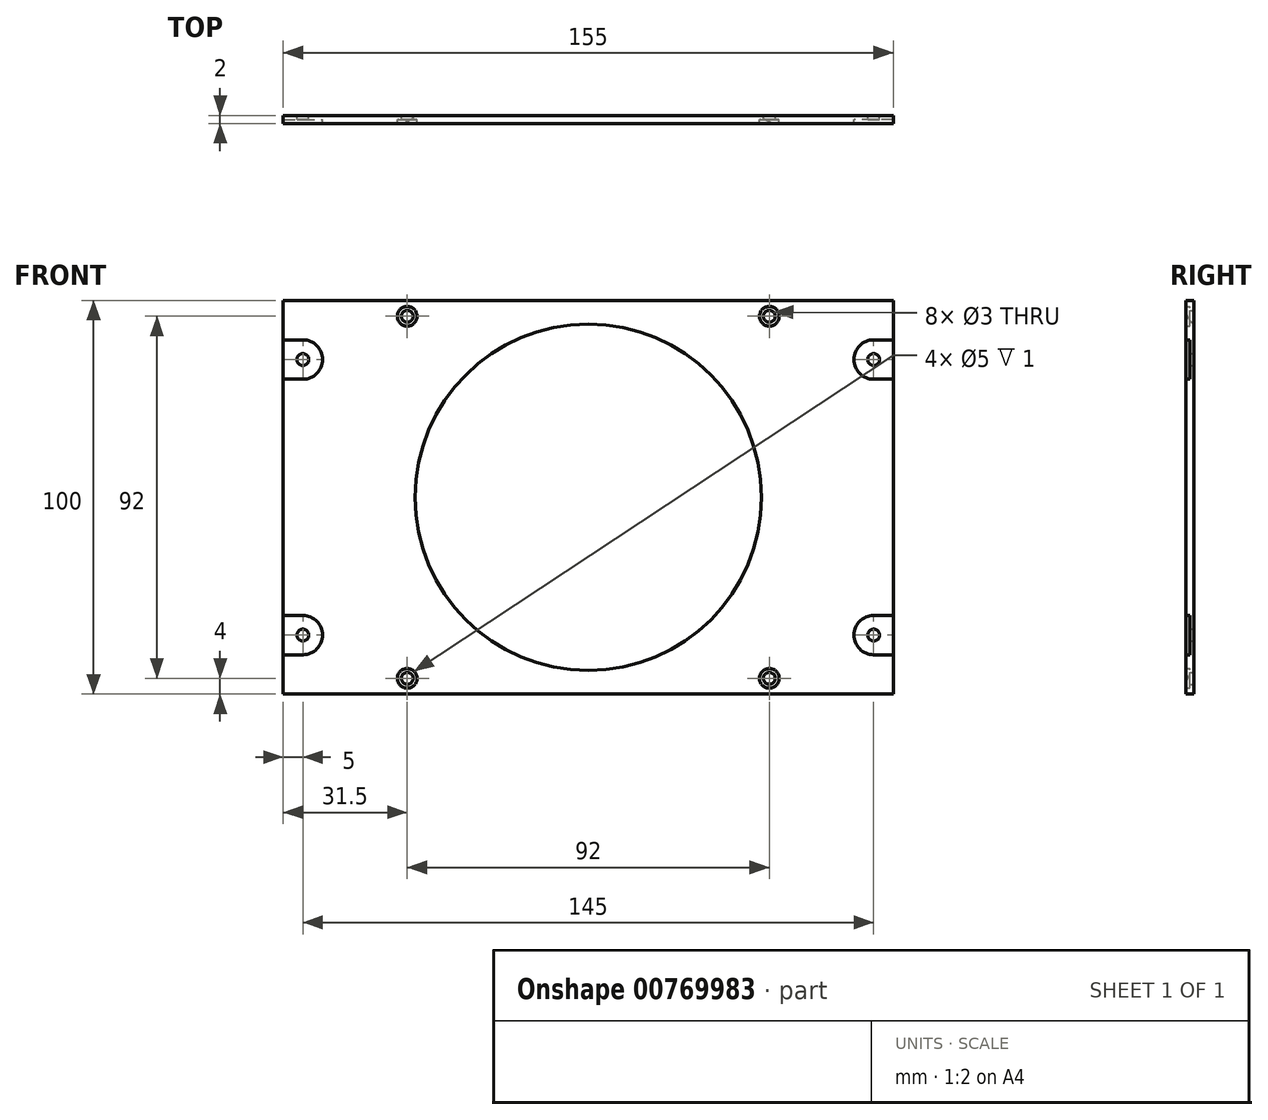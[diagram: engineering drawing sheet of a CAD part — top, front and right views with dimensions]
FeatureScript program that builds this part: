
annotation { "Feature Type Name" : "Feature", "Feature Type Description" : "" }
export const myFeature = defineFeature(function(context is Context, id is Id, definition is map)
    precondition{}
    {
        {
            var Q0;
            Q0=qCreatedBy(makeId("Front.planeOp"),FACE);
            var sketch = newSketch(context, id + "F0", { "sketchPlane" : qUnion([Q0])});
            skLineSegment(sketch, "E0.bottom", {"start": v(77.5, -50) * mm, "end": v(-77.5, -50) * mm});
            skLineSegment(sketch, "E0.top", {"start": v(77.5, 50) * mm, "end": v(-77.5, 50) * mm});
            skLineSegment(sketch, "E0.left", {"start": v(77.5, -50) * mm, "end": v(77.5, 50) * mm});
            skLineSegment(sketch, "E0.right", {"start": v(-77.5, -50) * mm, "end": v(-77.5, 50) * mm});
            skPoint(sketch, "E0.middle", {"position": v(0, 0) * mm});
            skCircle(sketch, "E1", {"center": v(0, 0) * mm, "radius": 44 * mm});
            skLineSegment(sketch, "E2.bottom", {"start": v(46, -46) * mm, "end": v(-46, -46) * mm});
            skLineSegment(sketch, "E2.top", {"start": v(46, 46) * mm, "end": v(-46, 46) * mm});
            skLineSegment(sketch, "E2.left", {"start": v(46, -46) * mm, "end": v(46, 46) * mm});
            skLineSegment(sketch, "E2.right", {"start": v(-46, -46) * mm, "end": v(-46, 46) * mm});
            skCircle(sketch, "E3", {"center": v(-46, 46) * mm, "radius": 1.5 * mm});
            skCircle(sketch, "E4", {"center": v(46, 46) * mm, "radius": 1.5 * mm});
            skCircle(sketch, "E5", {"center": v(46, -46) * mm, "radius": 1.5 * mm});
            skCircle(sketch, "E6", {"center": v(-46, -46) * mm, "radius": 1.5 * mm});
            skLineSegment(sketch, "E7.bottom", {"start": v(-77.5, 40) * mm, "end": v(-72.5, 40) * mm});
            skLineSegment(sketch, "E7.top", {"start": v(-77.5, 30) * mm, "end": v(-72.5, 30) * mm});
            skLineSegment(sketch, "E7.left", {"start": v(-77.5, 40) * mm, "end": v(-77.5, 30) * mm});
            skArc(sketch, "E8", {"start": v(-72.5, 40) * mm, "mid": v(-67.5, 35) * mm, "end": v(-72.5, 30) * mm});
            skLineSegment(sketch, "E9.MirrorCS", {"start": v(-77.5, -30) * mm, "end": v(-72.5, -30) * mm});
            skLineSegment(sketch, "E10.MirrorCS", {"start": v(-77.5, -40) * mm, "end": v(-72.5, -40) * mm});
            skArc(sketch, "E11.MirrorCS", {"start": v(-72.5, -40) * mm, "mid": v(-67.5, -35) * mm, "end": v(-72.5, -30) * mm});
            skLineSegment(sketch, "E12.MirrorCS", {"start": v(77.5, 40) * mm, "end": v(72.5, 40) * mm});
            skArc(sketch, "E13.MirrorCS", {"start": v(72.5, 40) * mm, "mid": v(67.5, 35) * mm, "end": v(72.5, 30) * mm});
            skLineSegment(sketch, "E14.MirrorCS", {"start": v(77.5, 30) * mm, "end": v(72.5, 30) * mm});
            skLineSegment(sketch, "E15.MirrorCS", {"start": v(77.5, -30) * mm, "end": v(72.5, -30) * mm});
            skLineSegment(sketch, "E16.MirrorCS", {"start": v(77.5, -40) * mm, "end": v(72.5, -40) * mm});
            skArc(sketch, "E17.MirrorCS", {"start": v(72.5, -40) * mm, "mid": v(67.5, -35) * mm, "end": v(72.5, -30) * mm});
            skCircle(sketch, "E18", {"center": v(-72.5, 35) * mm, "radius": 1.5 * mm});
            skCircle(sketch, "E19.MirrorC", {"center": v(-72.5, -35) * mm, "radius": 1.5 * mm});
            skCircle(sketch, "E20.MirrorC", {"center": v(72.5, 35) * mm, "radius": 1.5 * mm});
            skCircle(sketch, "E21.MirrorC", {"center": v(72.5, -35) * mm, "radius": 1.5 * mm});
            skCircle(sketch, "E22", {"center": v(-46, 46) * mm, "radius": 2.5 * mm});
            skCircle(sketch, "E23.MirrorC", {"center": v(-46, -46) * mm, "radius": 2.5 * mm});
            skCircle(sketch, "E24.MirrorC", {"center": v(46, -46) * mm, "radius": 2.5 * mm});
            skCircle(sketch, "E25.MirrorC", {"center": v(46, 46) * mm, "radius": 2.5 * mm});
            skSolve(sketch);
        }
        {
            var Q0;
            Q0=makeQuery(id+"F0.imprint","IMPRINT",FACE,{"disambiguationData":[TD([[makeQuery(id+"F0.imprint","IMPRINT",EDGE,{"derivedFrom":sQuery(id+"F0.wireOp",EDGE,"E0.bottom")}),-1.0]])]});
            var Q1;
            Q1=makeQuery(id+"F0.imprint","IMPRINT",FACE,{"disambiguationData":[TD([[makeQuery(id+"F0.imprint","IMPRINT",EDGE,{"derivedFrom":sQuery(id+"F0.wireOp",EDGE,"E1")}),-1.0]])]});
            extrude(context, id + "F1", {"entities" : qUnion([Q0, Q1]), "depth" : 2 * mm, "offsetDistance" : 25 * mm});
        }
        {
            var Q0;
            {var subQ0=sQuery(id+"F0.wireOp",EDGE,"E9.MirrorCS");Q0=makeQuery(id+"F0.imprint","IMPRINT",FACE,{"disambiguationData":[TD([[makeQuery(id+"F0.imprint","IMPRINT",EDGE,{"derivedFrom":subQ0}),-1.0]])]});}
            var Q1;
            Q1=makeQuery(id+"F0.imprint","IMPRINT",FACE,{"disambiguationData":[TD([[makeQuery(id+"F0.imprint","IMPRINT",EDGE,{"derivedFrom":sQuery(id+"F0.wireOp",EDGE,"E7.bottom")}),-1.0]])]});
            var Q2;
            {var subQ0=sQuery(id+"F0.wireOp",EDGE,"E12.MirrorCS");Q2=makeQuery(id+"F0.imprint","IMPRINT",FACE,{"disambiguationData":[TD([[makeQuery(id+"F0.imprint","IMPRINT",EDGE,{"derivedFrom":subQ0}),1.0]])]});}
            var Q3;
            {var subQ0=sQuery(id+"F0.wireOp",EDGE,"E15.MirrorCS");Q3=makeQuery(id+"F0.imprint","IMPRINT",FACE,{"disambiguationData":[TD([[makeQuery(id+"F0.imprint","IMPRINT",EDGE,{"derivedFrom":subQ0}),1.0]])]});}
            var Q4;
            {var subQ0=sQuery(id+"F0.wireOp",EDGE,"E22");var subQ1=sQuery(id+"F0.wireOp",EDGE,"E2.top");var subQ2=makeQuery(id+"F0.imprint","INTERSECT",VERTEX,{"derivedFrom":[subQ1,subQ0]});Q4=makeQuery(id+"F0.imprint","IMPRINT",FACE,{"disambiguationData":[TD([[makeQuery(id+"F0.imprint","IMPRINT",EDGE,{"disambiguationData":[TD([[subQ2,-1.0]])],"derivedFrom":subQ1}),-1.0]])]});}
            var Q5;
            {var subQ0=sQuery(id+"F0.wireOp",EDGE,"E22");var subQ1=sQuery(id+"F0.wireOp",EDGE,"E2.top");var subQ2=makeQuery(id+"F0.imprint","INTERSECT",VERTEX,{"derivedFrom":[subQ1,subQ0]});Q5=makeQuery(id+"F0.imprint","IMPRINT",FACE,{"disambiguationData":[TD([[makeQuery(id+"F0.imprint","IMPRINT",EDGE,{"disambiguationData":[TD([[subQ2,-1.0]])],"derivedFrom":subQ1}),1.0]])]});}
            var Q6;
            {var subQ0=sQuery(id+"F0.wireOp",EDGE,"E4");var subQ1=sQuery(id+"F0.wireOp",EDGE,"E2.top");var subQ2=makeQuery(id+"F0.imprint","INTERSECT",VERTEX,{"derivedFrom":[subQ1,subQ0]});Q6=makeQuery(id+"F0.imprint","IMPRINT",FACE,{"disambiguationData":[TD([[makeQuery(id+"F0.imprint","IMPRINT",EDGE,{"disambiguationData":[TD([[subQ2,-1.0]])],"derivedFrom":subQ1}),-1.0]])]});}
            var Q7;
            {var subQ0=sQuery(id+"F0.wireOp",EDGE,"E4");var subQ1=sQuery(id+"F0.wireOp",EDGE,"E2.top");var subQ2=makeQuery(id+"F0.imprint","INTERSECT",VERTEX,{"derivedFrom":[subQ1,subQ0]});Q7=makeQuery(id+"F0.imprint","IMPRINT",FACE,{"disambiguationData":[TD([[makeQuery(id+"F0.imprint","IMPRINT",EDGE,{"disambiguationData":[TD([[subQ2,-1.0]])],"derivedFrom":subQ1}),1.0]])]});}
            var Q8;
            {var subQ0=sQuery(id+"F0.wireOp",EDGE,"E5");var subQ1=sQuery(id+"F0.wireOp",EDGE,"E2.bottom");var subQ2=makeQuery(id+"F0.imprint","INTERSECT",VERTEX,{"derivedFrom":[subQ1,subQ0]});Q8=makeQuery(id+"F0.imprint","IMPRINT",FACE,{"disambiguationData":[TD([[makeQuery(id+"F0.imprint","IMPRINT",EDGE,{"disambiguationData":[TD([[subQ2,-1.0]])],"derivedFrom":subQ1}),1.0]])]});}
            var Q9;
            {var subQ0=sQuery(id+"F0.wireOp",EDGE,"E5");var subQ1=sQuery(id+"F0.wireOp",EDGE,"E2.bottom");var subQ2=makeQuery(id+"F0.imprint","INTERSECT",VERTEX,{"derivedFrom":[subQ1,subQ0]});Q9=makeQuery(id+"F0.imprint","IMPRINT",FACE,{"disambiguationData":[TD([[makeQuery(id+"F0.imprint","IMPRINT",EDGE,{"disambiguationData":[TD([[subQ2,-1.0]])],"derivedFrom":subQ1}),-1.0]])]});}
            var Q10;
            {var subQ0=sQuery(id+"F0.wireOp",EDGE,"E23.MirrorC");var subQ1=sQuery(id+"F0.wireOp",EDGE,"E2.bottom");var subQ2=makeQuery(id+"F0.imprint","INTERSECT",VERTEX,{"derivedFrom":[subQ1,subQ0]});Q10=makeQuery(id+"F0.imprint","IMPRINT",FACE,{"disambiguationData":[TD([[makeQuery(id+"F0.imprint","IMPRINT",EDGE,{"disambiguationData":[TD([[subQ2,-1.0]])],"derivedFrom":subQ1}),-1.0]])]});}
            var Q11;
            {var subQ0=sQuery(id+"F0.wireOp",EDGE,"E23.MirrorC");var subQ1=sQuery(id+"F0.wireOp",EDGE,"E2.bottom");var subQ2=makeQuery(id+"F0.imprint","INTERSECT",VERTEX,{"derivedFrom":[subQ1,subQ0]});Q11=makeQuery(id+"F0.imprint","IMPRINT",FACE,{"disambiguationData":[TD([[makeQuery(id+"F0.imprint","IMPRINT",EDGE,{"disambiguationData":[TD([[subQ2,-1.0]])],"derivedFrom":subQ1}),1.0]])]});}
            extrude(context, id + "F2", {"entities" : qUnion([Q0, Q1, Q2, Q3, Q4, Q5, Q6, Q7, Q8, Q9, Q10, Q11]), "operationType" : NewBodyOperationType.ADD, "depth" : 1 * mm, "offsetDistance" : 25 * mm});
        }
        {
            var Q0;
            Q0=makeQuery(id+"F1.opExtrude","CAP_EDGE",EDGE,{"disambiguationData":[OSD([sQuery(id+"F0.wireOp",EDGE,"E1")])],"isStart":false});
            fillet(context, id + "F3", {"entities" : qUnion([Q0]), "radius" : 5 * mm, "tangentPropagation" : true, "allowEdgeOverflow" : false});
        }
    });
